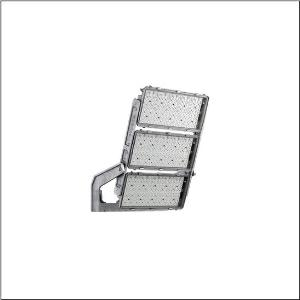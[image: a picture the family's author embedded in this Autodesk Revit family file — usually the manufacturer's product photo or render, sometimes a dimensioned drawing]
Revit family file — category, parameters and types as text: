
# Revit family: floodlight_fl_11_maxi_pro_remote___pl33tblc_5xa779426h01aa_354a
name_source: partatom
category: Lighting Fixtures
units: mm (PartAtom-declared; Revit-internal decimal feet)

## family parameters
Cut with Voids When Loaded = No
Host = Face
Light Source = No
Part Type = Normal
Room Calculation Point = No
Round Connector Dimension = Use Diameter
Shared = No

## types (1)
- --- (1 x LED, 124720 lm, 1388.3 W, 4000K)
    Apparent Load = 1388 VA
    CIE Flux Codes = 24 77 100 100 100
    Color Rendering = 70
    Color Temperature = 4000K
    Default Elevation = 1800 mm
    Description = Floodlight FL 11  maxi  pro Remote floodlight; light control with lens of PMMA; cover panel of toughened safety glass, transparent; light distribution: PL33TBLC, asymmetric direct distribution, LEDcolour temperature: 4000K, rated luminous flux: 124.720lm, colour rendering: CRI > 70, light colour: 740; luminous efficacy: 90lm/W; brightness control: DALI 2 (1 DALI address); with terminal, 8-pole, max. 2.5mm², mains connection: 220..240V/380..400V AC, 50/60Hz, surge voltage resistance: line to ground: 10kV, ECG replaceable separately, LED unit replaceable without ESD environment, dustproof LED module, dimming range 10..100%, no afterglow with DALI off / DMX off command; 1388W floodlight with 2x LED unit of diecast aluminium, coated grey; length: 713mm / width: 651mm / height: 338mm; mounting bracket, of diecast aluminium, uncoated, natural, equipment: Power, protection rating (complete): IP66; insulation class (complete): insulation class I (protective earthing); certification: CE, ENEC, VDE; ball protection: ball impact resistance with accessories, impact resistance: IK07; rated ambient temperature 10°C, only for outdoor installations, permissible operating ambient temperature: -40..+30°C, permissible storage temperature: -40..+85°C; packaging unit: 1 piece

Light Distribution: PL33TBLC
    Height = 320 mm
    Lamp = 1 x LED
    Lamp Light Flux = 124720 lm
    Lamp Power = 1388.3 W
    Lamp count = 1
    Length = 1002 mm
    Luminous efficacy = 90 lm/W
    Manufacturer = Siteco
    ModVariant = No
    Model = 5XA779426H01AA
    Mounting Place = Ceiling
    Mounting Type = Surface mounted
    Number of Poles = 1
    OnlyDefault = Yes
    Power Factor = 1
    Product Name = Floodlight FL 11 maxi pro Remote | PL33TBLC
    Product group = floodlight | ceiling mounted
    ProductGroupID = 302
    Protection Class = Protection class I
    Protection Degree = IP 66
    RLX_Detail_Level = 1
    RLX_Emergency_Light_Flux = 0 lm
    RLX_Emergency_Type = 0
    RLX_Emergency_Type_DB = No
    RlxData = <blob elided: 52221 chars, md5=690f3220>
    Socket = socket
    Standby Power = 0 W
    System Light Flux = 124720 lm
    System Power = 1388 W
    Type Comments = factory setting: luminous flux: 100 % | dim-lin: 254 | 955 mA
    Type Image = l_1006784.jpg
    URL = http://relux.com
    VarID = @adj_064855
    Voltage = 0 V
    Weight = 0.00 kg
    Width = 655 mm

## geometry (parser evidence)
native form markers: Blend x4, Sweep x15
no freeform markers — native parametric forms only
